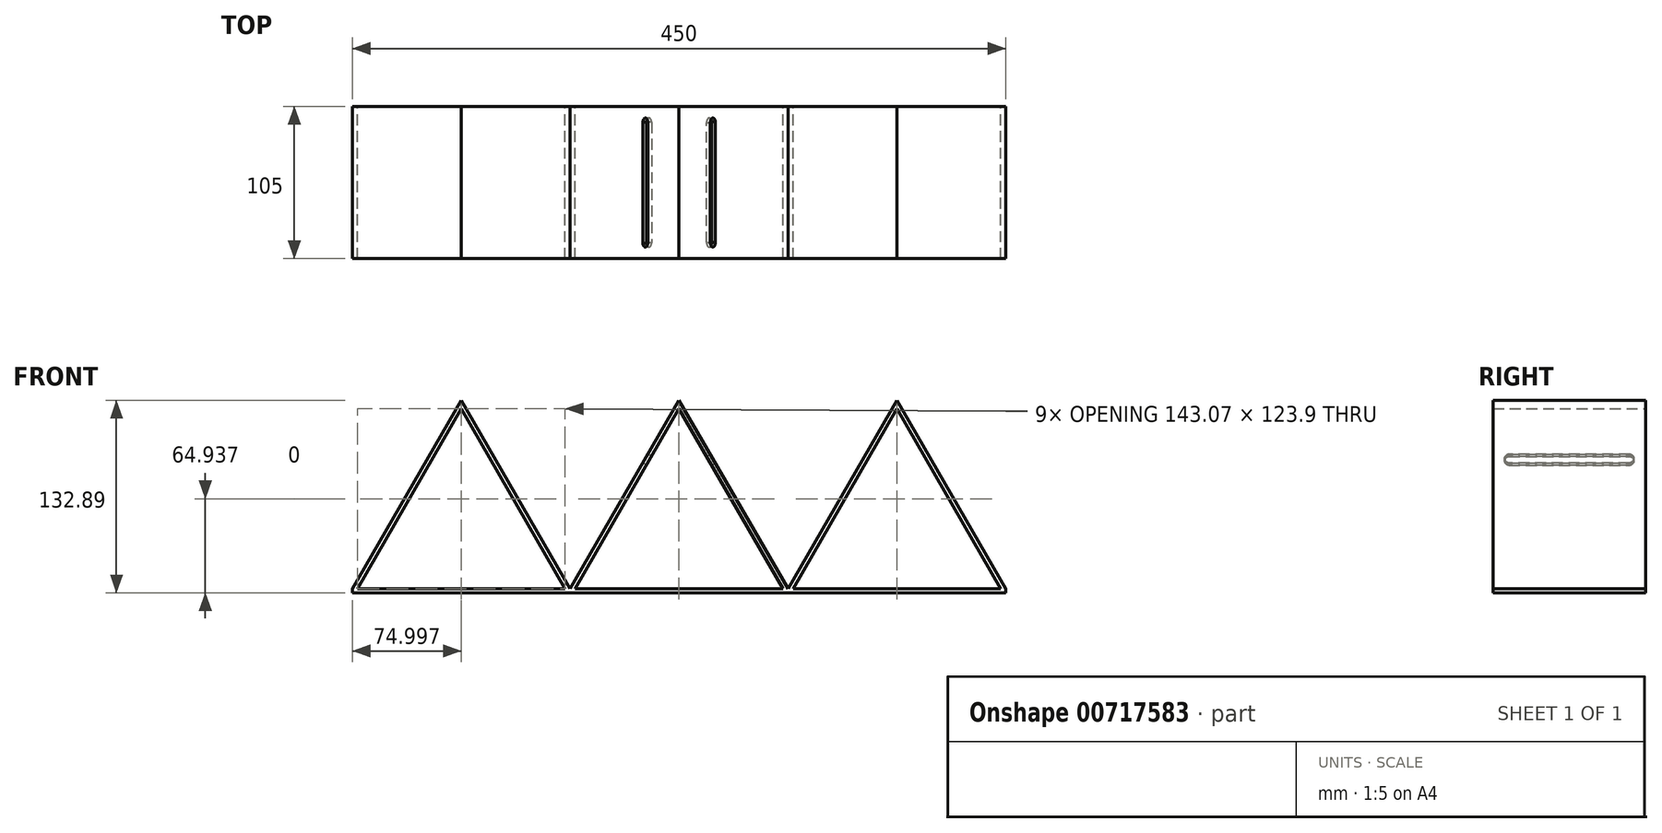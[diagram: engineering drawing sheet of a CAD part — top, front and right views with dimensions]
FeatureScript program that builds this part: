
annotation { "Feature Type Name" : "Feature", "Feature Type Description" : "" }
export const myFeature = defineFeature(function(context is Context, id is Id, definition is map)
    precondition{}
    {
        {
            var Q0;
            Q0=qCreatedBy(makeId("Front.planeOp"),FACE);
            var sketch = newSketch(context, id + "F0", { "sketchPlane" : qUnion([Q0])});
            skLineSegment(sketch, "E0", {"start": v(-43.41, -91.2) * mm, "end": v(406.59, -91.2) * mm});
            skLineSegment(sketch, "E1", {"start": v(31.59, 38.7) * mm, "end": v(-43.41, -91.2) * mm});
            skLineSegment(sketch, "E2", {"start": v(31.59, 38.7) * mm, "end": v(106.59, -91.2) * mm});
            skLineSegment(sketch, "E3", {"start": v(106.59, -91.2) * mm, "end": v(181.59, 38.7) * mm});
            skLineSegment(sketch, "E4", {"start": v(181.59, 38.7) * mm, "end": v(256.59, -91.2) * mm});
            skLineSegment(sketch, "E5", {"start": v(256.59, -91.2) * mm, "end": v(331.59, 38.7) * mm});
            skLineSegment(sketch, "E6", {"start": v(331.59, 38.7) * mm, "end": v(406.59, -91.2) * mm});
            skLineSegment(sketch, "E7.0", {"start": v(-43.4, -94.18) * mm, "end": v(406.59, -94.18) * mm});
            skLineSegment(sketch, "E8.0", {"start": v(-43.65, -94.2) * mm, "end": v(406.35, -94.2) * mm});
            skLineSegment(sketch, "E9", {"start": v(-43.41, -91.2) * mm, "end": v(-43.4, -94.18) * mm});
            skLineSegment(sketch, "E10", {"start": v(406.59, -91.2) * mm, "end": v(406.59, -94.18) * mm});
            skLineSegment(sketch, "E11.0", {"start": v(31.59, 32.7) * mm, "end": v(-39.95, -91.2) * mm});
            skLineSegment(sketch, "E11.1", {"start": v(31.59, 32.7) * mm, "end": v(103.12, -91.2) * mm});
            skLineSegment(sketch, "E12.0", {"start": v(181.59, 32.7) * mm, "end": v(253.12, -91.2) * mm});
            skLineSegment(sketch, "E12.1", {"start": v(110.05, -91.2) * mm, "end": v(181.59, 32.7) * mm});
            skLineSegment(sketch, "E13.0", {"start": v(331.59, 32.7) * mm, "end": v(403.12, -91.2) * mm});
            skLineSegment(sketch, "E13.1", {"start": v(260.05, -91.2) * mm, "end": v(331.59, 32.7) * mm});
            skSolve(sketch);
        }
        {
            var Q0;
            Q0=makeQuery(id+"F0.imprint","IMPRINT",FACE,{"disambiguationData":[TD([[makeQuery(id+"F0.imprint","IMPRINT",EDGE,{"derivedFrom":sQuery(id+"F0.wireOp",EDGE,"E0")}),1.0]])]});
            var Q1;
            Q1=makeQuery(id+"F0.imprint","IMPRINT",FACE,{"disambiguationData":[TD([[makeQuery(id+"F0.imprint","IMPRINT",EDGE,{"derivedFrom":sQuery(id+"F0.wireOp",EDGE,"E7.0")}),1.0]])]});
            extrude(context, id + "F1", {"entities" : qUnion([Q0, Q1]), "depth" : 105 * mm, "offsetDistance" : 25 * mm});
        }
        {
            var Q0;
            Q0=makeQuery(id+"F1.opExtrude","SWEPT_FACE",FACE,{"disambiguationData":[OSD([sQuery(id+"F0.wireOp",EDGE,"E4")])]});
            var sketch = newSketch(context, id + "F2", { "sketchPlane" : qUnion([Q0])});
            skLineSegment(sketch, "E14", {"start": v(-105, -100.27) * mm, "end": v(0, -100.27) * mm});
            skLineSegment(sketch, "E15", {"start": v(-105, -107.27) * mm, "end": v(0, -107.27) * mm});
            skArc(sketch, "E16", {"start": v(-93.9, -100.27) * mm, "mid": v(-97, -103.77) * mm, "end": v(-93.9, -107.27) * mm});
            skArc(sketch, "E17", {"start": v(-10.66, -107.27) * mm, "mid": v(-8.01, -103.5) * mm, "end": v(-11.28, -100.27) * mm});
            skSolve(sketch);
        }
        {
            var Q0;
            Q0=makeQuery(id+"F1.opExtrude","SWEPT_FACE",FACE,{"disambiguationData":[OSD([sQuery(id+"F0.wireOp",EDGE,"E3")])]});
            var sketch = newSketch(context, id + "F3", { "sketchPlane" : qUnion([Q0])});
            skLineSegment(sketch, "E18", {"start": v(0, 81.32) * mm, "end": v(105, 81.32) * mm});
            skLineSegment(sketch, "E19", {"start": v(0, 74.32) * mm, "end": v(105, 74.32) * mm});
            skArc(sketch, "E20", {"start": v(10.88, 81.32) * mm, "mid": v(8, 77.76) * mm, "end": v(11.02, 74.32) * mm});
            skArc(sketch, "E21", {"start": v(94.23, 74.32) * mm, "mid": v(97, 77.93) * mm, "end": v(93.96, 81.32) * mm});
            skSolve(sketch);
        }
        {
            var Q0;
            Q0 = qSketchRegion(id + "F2", true);
            extrude(context, id + "F4", {"entities" : qUnion([Q0]), "operationType" : NewBodyOperationType.REMOVE, "depth" : -3 * mm, "offsetDistance" : 25 * mm});
        }
        {
            var Q0;
            Q0 = qSketchRegion(id + "F3", true);
            extrude(context, id + "F5", {"entities" : qUnion([Q0]), "operationType" : NewBodyOperationType.REMOVE, "oppositeDirection" : true, "depth" : 3.2 * mm, "offsetDistance" : 25 * mm});
        }
    });
